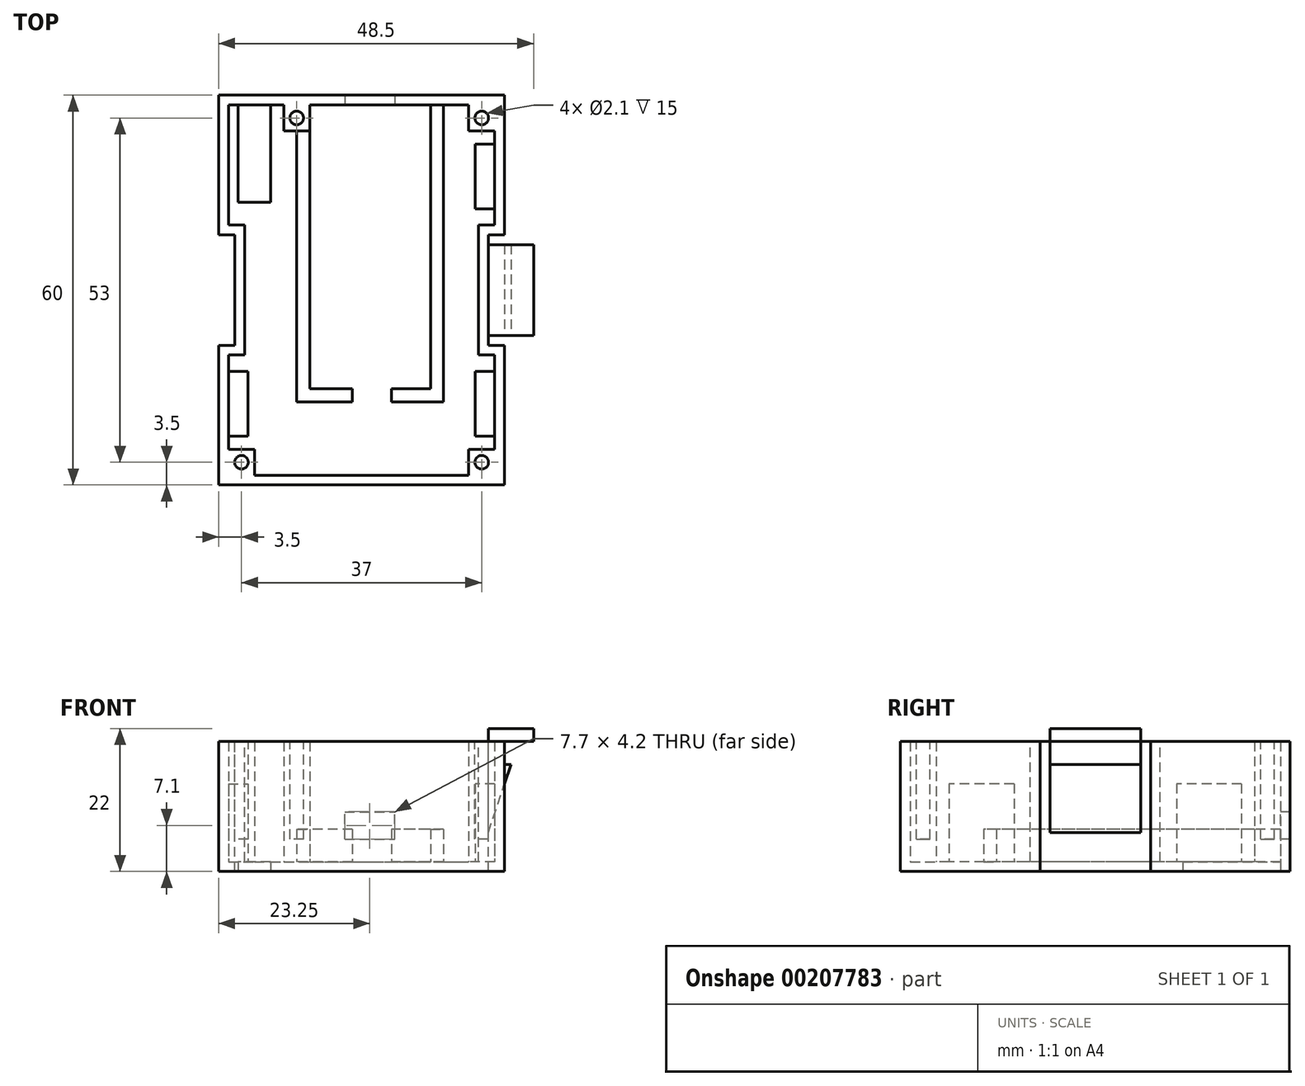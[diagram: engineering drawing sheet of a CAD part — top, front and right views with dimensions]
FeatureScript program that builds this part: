
annotation { "Feature Type Name" : "Feature", "Feature Type Description" : "" }
export const myFeature = defineFeature(function(context is Context, id is Id, definition is map)
    precondition{}
    {
        {
            var Q0;
            Q0=qCreatedBy(makeId("Top.planeOp"),FACE);
            var sketch = newSketch(context, id + "F0", { "sketchPlane" : qUnion([Q0])});
            skLineSegment(sketch, "E0.bottom", {"start": v(-22, 30) * mm, "end": v(22, 30) * mm});
            skLineSegment(sketch, "E0.top", {"start": v(-22, -30) * mm, "end": v(22, -30) * mm});
            skLineSegment(sketch, "E0.left", {"start": v(-22, 30) * mm, "end": v(-22, -30) * mm});
            skLineSegment(sketch, "E0.right", {"start": v(22, 30) * mm, "end": v(22, -30) * mm});
            skSolve(sketch);
        }
        {
            var Q0;
            Q0 = qSketchRegion(id + "F0", true);
            extrude(context, id + "F1", {"entities" : qUnion([Q0]), "depth" : 20 * mm});
        }
        {
            var Q0;
            Q0=makeQuery(id+"F1.opExtrude","CAP_FACE",FACE,{"disambiguationData":[OSD([sQuery(id+"F0.wireOp",EDGE,"E0.bottom"),sQuery(id+"F0.wireOp",EDGE,"E0.top"),sQuery(id+"F0.wireOp",EDGE,"E0.left"),sQuery(id+"F0.wireOp",EDGE,"E0.right")])],"isStart":false});
            var sketch = newSketch(context, id + "F2", { "sketchPlane" : qUnion([Q0])});
            skLineSegment(sketch, "E1.bottom", {"start": v(22, 8.5) * mm, "end": v(19.5, 8.5) * mm});
            skLineSegment(sketch, "E1.top", {"start": v(22, -8.5) * mm, "end": v(19.5, -8.5) * mm});
            skLineSegment(sketch, "E1.left", {"start": v(22, 8.5) * mm, "end": v(22, -8.5) * mm});
            skLineSegment(sketch, "E1.right", {"start": v(19.5, 8.5) * mm, "end": v(19.5, -8.5) * mm});
            skLineSegment(sketch, "E2.bottom", {"start": v(-22, 8.5) * mm, "end": v(-19.5, 8.5) * mm});
            skLineSegment(sketch, "E2.top", {"start": v(-22, -8.5) * mm, "end": v(-19.5, -8.5) * mm});
            skLineSegment(sketch, "E2.left", {"start": v(-22, 8.5) * mm, "end": v(-22, -8.5) * mm});
            skLineSegment(sketch, "E2.right", {"start": v(-19.5, 8.5) * mm, "end": v(-19.5, -8.5) * mm});
            skSolve(sketch);
        }
        {
            var Q0;
            Q0 = qSketchRegion(id + "F2", true);
            extrude(context, id + "F3", {"entities" : qUnion([Q0]), "operationType" : NewBodyOperationType.REMOVE, "oppositeDirection" : true, "depth" : 20 * mm});
        }
        {
            var Q0;
            Q0=makeQuery(id+"F1.opExtrude","CAP_FACE",FACE,{"disambiguationData":[OSD([sQuery(id+"F0.wireOp",EDGE,"E0.bottom"),sQuery(id+"F0.wireOp",EDGE,"E0.top"),sQuery(id+"F0.wireOp",EDGE,"E0.left"),sQuery(id+"F0.wireOp",EDGE,"E0.right")])],"isStart":false});
            shell(context, id + "F4", {"entities" : qUnion([Q0]), "thickness" : 1.5 * mm});
        }
        {
            var Q0;
            Q0=makeQuery(id+"F1.opExtrude","CAP_FACE",FACE,{"disambiguationData":[OSD([sQuery(id+"F0.wireOp",EDGE,"E0.bottom"),sQuery(id+"F0.wireOp",EDGE,"E0.top"),sQuery(id+"F0.wireOp",EDGE,"E0.left"),sQuery(id+"F0.wireOp",EDGE,"E0.right")])],"isStart":true});
            var sketch = newSketch(context, id + "F5", { "sketchPlane" : qUnion([Q0])});
            skLineSegment(sketch, "E3.bottom", {"start": v(-19, -28.5) * mm, "end": v(-14, -28.5) * mm});
            skLineSegment(sketch, "E3.top", {"start": v(-19, -13.5) * mm, "end": v(-14, -13.5) * mm});
            skLineSegment(sketch, "E3.left", {"start": v(-19, -28.5) * mm, "end": v(-19, -13.5) * mm});
            skLineSegment(sketch, "E3.right", {"start": v(-14, -28.5) * mm, "end": v(-14, -13.5) * mm});
            skSolve(sketch);
        }
        {
            var Q0;
            Q0 = qSketchRegion(id + "F5", true);
            extrude(context, id + "F6", {"entities" : qUnion([Q0]), "operationType" : NewBodyOperationType.REMOVE, "oppositeDirection" : true, "depth" : 2 * mm});
        }
        {
            var Q0;
            Q0=makeQuery(id+"F3.boolean.opBoolean","COPY",FACE,{"derivedFrom":makeQuery(id+"F3.opExtrude","SWEPT_FACE",FACE,{"disambiguationData":[OSD([sQuery(id+"F2.wireOp",EDGE,"E1.right")])]})});
            var sketch = newSketch(context, id + "F7", { "sketchPlane" : qUnion([Q0])});
            skLineSegment(sketch, "E4.bottom", {"start": v(-7, 20) * mm, "end": v(7, 20) * mm});
            skLineSegment(sketch, "E4.top", {"start": v(-7, 6) * mm, "end": v(7, 6) * mm});
            skLineSegment(sketch, "E4.left", {"start": v(-7, 20) * mm, "end": v(-7, 6) * mm});
            skLineSegment(sketch, "E4.right", {"start": v(7, 20) * mm, "end": v(7, 6) * mm});
            skLineSegment(sketch, "E5.top", {"start": v(-7, 22) * mm, "end": v(7, 22) * mm});
            skLineSegment(sketch, "E5.left", {"start": v(-7, 20) * mm, "end": v(-7, 22) * mm});
            skLineSegment(sketch, "E5.right", {"start": v(7, 20) * mm, "end": v(7, 22) * mm});
            skSolve(sketch);
        }
        {
            var Q0;
            Q0 = qSketchRegion(id + "F7", true);
            extrude(context, id + "F8", {"entities" : qUnion([Q0]), "operationType" : NewBodyOperationType.ADD, "depth" : 7 * mm});
        }
        {
            var Q0;
            Q0=makeQuery(id+"F8.opExtrude","SWEPT_FACE",FACE,{"disambiguationData":[OSD([sQuery(id+"F7.wireOp",EDGE,"E4.left"),sQuery(id+"F7.wireOp",EDGE,"E5.left")])]});
            var sketch = newSketch(context, id + "F9", { "sketchPlane" : qUnion([Q0])});
            skLineSegment(sketch, "E6", {"start": v(19.5, 6) * mm, "end": v(23, 16.5) * mm});
            skLineSegment(sketch, "E7", {"start": v(23, 16.5) * mm, "end": v(22, 16.5) * mm});
            skLineSegment(sketch, "E8", {"start": v(22, 16.5) * mm, "end": v(22, 20) * mm});
            skLineSegment(sketch, "E9", {"start": v(22, 20) * mm, "end": v(26.5, 20) * mm});
            skLineSegment(sketch, "E10", {"start": v(26.5, 20) * mm, "end": v(26.5, 6) * mm});
            skLineSegment(sketch, "E11", {"start": v(26.5, 6) * mm, "end": v(19.5, 6) * mm});
            skSolve(sketch);
        }
        {
            var Q0;
            Q0 = qSketchRegion(id + "F9", true);
            extrude(context, id + "F10", {"entities" : qUnion([Q0]), "operationType" : NewBodyOperationType.REMOVE, "oppositeDirection" : true, "depth" : 14 * mm});
        }
        {
            var Q0;
            Q0=makeQuery(id+"F4.opShell","OFFSET_FACE",FACE,{"disambiguationData":[OSD([sQuery(id+"F0.wireOp",EDGE,"E0.bottom"),sQuery(id+"F0.wireOp",EDGE,"E0.top"),sQuery(id+"F0.wireOp",EDGE,"E0.left"),sQuery(id+"F0.wireOp",EDGE,"E0.right")])]});
            var sketch = newSketch(context, id + "F11", { "sketchPlane" : qUnion([Q0])});
            skLineSegment(sketch, "E12.bottom", {"start": v(20.5, 28.5) * mm, "end": v(16.5, 28.5) * mm});
            skLineSegment(sketch, "E12.top", {"start": v(20.5, 24.5) * mm, "end": v(16.5, 24.5) * mm});
            skLineSegment(sketch, "E12.left", {"start": v(20.5, 28.5) * mm, "end": v(20.5, 24.5) * mm});
            skLineSegment(sketch, "E12.right", {"start": v(16.5, 28.5) * mm, "end": v(16.5, 24.5) * mm});
            skLineSegment(sketch, "E13.bottom", {"start": v(20.5, -28.5) * mm, "end": v(16.5, -28.5) * mm});
            skLineSegment(sketch, "E13.top", {"start": v(20.5, -24.5) * mm, "end": v(16.5, -24.5) * mm});
            skLineSegment(sketch, "E13.left", {"start": v(20.5, -28.5) * mm, "end": v(20.5, -24.5) * mm});
            skLineSegment(sketch, "E13.right", {"start": v(16.5, -28.5) * mm, "end": v(16.5, -24.5) * mm});
            skLineSegment(sketch, "E14.bottom", {"start": v(-20.5, -28.5) * mm, "end": v(-16.5, -28.5) * mm});
            skLineSegment(sketch, "E14.top", {"start": v(-20.5, -24.5) * mm, "end": v(-16.5, -24.5) * mm});
            skLineSegment(sketch, "E14.left", {"start": v(-20.5, -28.5) * mm, "end": v(-20.5, -24.5) * mm});
            skLineSegment(sketch, "E14.right", {"start": v(-16.5, -28.5) * mm, "end": v(-16.5, -24.5) * mm});
            skLineSegment(sketch, "E15.bottom", {"start": v(-12, 28.5) * mm, "end": v(-8, 28.5) * mm});
            skLineSegment(sketch, "E15.top", {"start": v(-12, 24.5) * mm, "end": v(-8, 24.5) * mm});
            skLineSegment(sketch, "E15.left", {"start": v(-12, 28.5) * mm, "end": v(-12, 24.5) * mm});
            skLineSegment(sketch, "E15.right", {"start": v(-8, 28.5) * mm, "end": v(-8, 24.5) * mm});
            skSolve(sketch);
        }
        {
            var Q0;
            Q0 = qSketchRegion(id + "F11", true);
            var Q1;
            Q1=makeQuery(id+"F1.opExtrude","CAP_FACE",FACE,{"disambiguationData":[OSD([sQuery(id+"F0.wireOp",EDGE,"E0.bottom"),sQuery(id+"F0.wireOp",EDGE,"E0.top"),sQuery(id+"F0.wireOp",EDGE,"E0.left"),sQuery(id+"F0.wireOp",EDGE,"E0.right")])],"isStart":false});
            extrude(context, id + "F12", {"entities" : qUnion([Q0]), "operationType" : NewBodyOperationType.ADD, "endBound" : BoundingType.UP_TO_SURFACE, "endBoundEntityFace" : qUnion([Q1]), "depth" : 18.5 * mm});
        }
        {
            var Q0;
            {var subQ0=sQuery(id+"F0.wireOp",EDGE,"E0.right");var subQ1=sQuery(id+"F0.wireOp",EDGE,"E0.left");var subQ2=sQuery(id+"F0.wireOp",EDGE,"E0.top");var subQ3=sQuery(id+"F0.wireOp",EDGE,"E0.bottom");Q0=makeQuery(id+"F12.boolean.opBoolean","MERGE",FACE,{"derivedFrom":[makeQuery(id+"F1.opExtrude","CAP_FACE",FACE,{"disambiguationData":[OSD([subQ3,subQ2,subQ1,subQ0])],"isStart":false}),makeQuery(id+"F12.opExtrude","CAP_FACE",FACE,{"disambiguationData":[OSD([subQ3,subQ2,subQ1,subQ0]),ownerDisambiguation([makeQuery(id+"F12.opExtrude","SWEPT_BODY",BODY,{"disambiguationData":[OSD([sQuery(id+"F11.wireOp",EDGE,"E12.bottom"),sQuery(id+"F11.wireOp",EDGE,"E12.top"),sQuery(id+"F11.wireOp",EDGE,"E12.left"),sQuery(id+"F11.wireOp",EDGE,"E12.right")])]})])],"isStart":false}),makeQuery(id+"F12.opExtrude","CAP_FACE",FACE,{"disambiguationData":[OSD([subQ3,subQ2,subQ1,subQ0]),ownerDisambiguation([makeQuery(id+"F12.opExtrude","SWEPT_BODY",BODY,{"disambiguationData":[OSD([sQuery(id+"F11.wireOp",EDGE,"E13.bottom"),sQuery(id+"F11.wireOp",EDGE,"E13.top"),sQuery(id+"F11.wireOp",EDGE,"E13.left"),sQuery(id+"F11.wireOp",EDGE,"E13.right")])]})])],"isStart":false}),makeQuery(id+"F12.opExtrude","CAP_FACE",FACE,{"disambiguationData":[OSD([subQ3,subQ2,subQ1,subQ0]),ownerDisambiguation([makeQuery(id+"F12.opExtrude","SWEPT_BODY",BODY,{"disambiguationData":[OSD([sQuery(id+"F11.wireOp",EDGE,"E14.bottom"),sQuery(id+"F11.wireOp",EDGE,"E14.top"),sQuery(id+"F11.wireOp",EDGE,"E14.left"),sQuery(id+"F11.wireOp",EDGE,"E14.right")])]})])],"isStart":false}),makeQuery(id+"F12.opExtrude","CAP_FACE",FACE,{"disambiguationData":[OSD([subQ3,subQ2,subQ1,subQ0]),ownerDisambiguation([makeQuery(id+"F12.opExtrude","SWEPT_BODY",BODY,{"disambiguationData":[OSD([sQuery(id+"F11.wireOp",EDGE,"E15.bottom"),sQuery(id+"F11.wireOp",EDGE,"E15.top"),sQuery(id+"F11.wireOp",EDGE,"E15.left"),sQuery(id+"F11.wireOp",EDGE,"E15.right")])]})])],"isStart":false})]});}
            var sketch = newSketch(context, id + "F13", { "sketchPlane" : qUnion([Q0])});
            skCircle(sketch, "E16", {"center": v(-10, 26.5) * mm, "radius": 1.05 * mm});
            skPoint(sketch, "E16.centerSnap0", {"position": v(-12, 26.5) * mm});
            skCircle(sketch, "E17", {"center": v(18.5, 26.5) * mm, "radius": 1.05 * mm});
            skPoint(sketch, "E17.centerSnap0", {"position": v(18.5, 24.5) * mm});
            skPoint(sketch, "E17.centerSnap1", {"position": v(16.5, 26.5) * mm});
            skCircle(sketch, "E18", {"center": v(18.5, -26.5) * mm, "radius": 1.05 * mm});
            skPoint(sketch, "E18.centerSnap0", {"position": v(16.5, -26.5) * mm});
            skPoint(sketch, "E18.centerSnap1", {"position": v(18.5, -24.5) * mm});
            skCircle(sketch, "E19", {"center": v(-18.5, -26.5) * mm, "radius": 1.05 * mm});
            skPoint(sketch, "E19.centerSnap0", {"position": v(-16.5, -26.5) * mm});
            skPoint(sketch, "E19.centerSnap1", {"position": v(-18.5, -24.5) * mm});
            skPoint(sketch, "E20", {"position": v(-10, 24.5) * mm});
            skSolve(sketch);
        }
        {
            var Q0;
            Q0 = qSketchRegion(id + "F13", true);
            extrude(context, id + "F14", {"entities" : qUnion([Q0]), "operationType" : NewBodyOperationType.REMOVE, "oppositeDirection" : true, "depth" : 15 * mm});
        }
        {
            var Q0;
            {var subQ4=sQuery(id+"F0.wireOp",EDGE,"E0.bottom");var subQ5=sQuery(id+"F11.wireOp",EDGE,"E12.right");Q0=makeQuery(id+"F12.boolean.opBoolean","SPLIT",FACE,{"disambiguationData":[TD([makeQuery(id+"F12.opExtrude","SWEPT_FACE",FACE,{"disambiguationData":[OSD([subQ5])]})])],"derivedFrom":makeQuery(id+"F6.boolean.opBoolean","MERGE",FACE,{"derivedFrom":[makeQuery(id+"F4.opShell","OFFSET_FACE",FACE,{"disambiguationData":[OSD([subQ4])]}),makeQuery(id+"F6.opExtrude","SWEPT_FACE",FACE,{"disambiguationData":[OSD([sQuery(id+"F5.wireOp",EDGE,"E3.bottom")])]})]})});}
            var sketch = newSketch(context, id + "F15", { "sketchPlane" : qUnion([Q0])});
            skLineSegment(sketch, "E21.bottom", {"start": v(-2.6, 5) * mm, "end": v(5.1, 5) * mm});
            skLineSegment(sketch, "E21.top", {"start": v(-2.6, 9.2) * mm, "end": v(5.1, 9.2) * mm});
            skLineSegment(sketch, "E21.left", {"start": v(-2.6, 5) * mm, "end": v(-2.6, 9.2) * mm});
            skLineSegment(sketch, "E21.right", {"start": v(5.1, 5) * mm, "end": v(5.1, 9.2) * mm});
            skSolve(sketch);
        }
        {
            var Q0;
            Q0 = qSketchRegion(id + "F15", true);
            extrude(context, id + "F16", {"entities" : qUnion([Q0]), "operationType" : NewBodyOperationType.REMOVE, "endBound" : BoundingType.UP_TO_NEXT, "oppositeDirection" : true, "depth" : 25 * mm});
        }
        {
            var Q0;
            Q0=makeQuery(id+"F4.opShell","OFFSET_FACE",FACE,{"disambiguationData":[OSD([sQuery(id+"F0.wireOp",EDGE,"E0.bottom"),sQuery(id+"F0.wireOp",EDGE,"E0.top"),sQuery(id+"F0.wireOp",EDGE,"E0.left"),sQuery(id+"F0.wireOp",EDGE,"E0.right")])]});
            var sketch = newSketch(context, id + "F17", { "sketchPlane" : qUnion([Q0])});
            skLineSegment(sketch, "E22.bottom", {"start": v(10.6, 28.5) * mm, "end": v(12.6, 28.5) * mm});
            skLineSegment(sketch, "E22.top", {"start": v(10.6, -15.2) * mm, "end": v(12.6, -15.2) * mm});
            skLineSegment(sketch, "E22.left", {"start": v(10.6, 28.5) * mm, "end": v(10.6, -15.2) * mm});
            skLineSegment(sketch, "E22.right", {"start": v(12.6, 28.5) * mm, "end": v(12.6, -15.2) * mm});
            skLineSegment(sketch, "E23.bottom", {"start": v(-8, 24.5) * mm, "end": v(-10, 24.5) * mm});
            skLineSegment(sketch, "E23.top", {"start": v(-8, -15.2) * mm, "end": v(-10, -15.2) * mm});
            skLineSegment(sketch, "E23.left", {"start": v(-8, 24.5) * mm, "end": v(-8, -15.2) * mm});
            skLineSegment(sketch, "E23.right", {"start": v(-10, 24.5) * mm, "end": v(-10, -15.2) * mm});
            skLineSegment(sketch, "E24.bottom", {"start": v(12.6, -15.2) * mm, "end": v(-10, -15.2) * mm});
            skLineSegment(sketch, "E24.top", {"start": v(12.6, -17.2) * mm, "end": v(-10, -17.2) * mm});
            skLineSegment(sketch, "E24.left", {"start": v(12.6, -15.2) * mm, "end": v(12.6, -17.2) * mm});
            skLineSegment(sketch, "E24.right", {"start": v(-10, -15.2) * mm, "end": v(-10, -17.2) * mm});
            skSolve(sketch);
        }
        {
            var Q0;
            Q0 = qSketchRegion(id + "F17", true);
            extrude(context, id + "F18", {"entities" : qUnion([Q0]), "operationType" : NewBodyOperationType.ADD, "depth" : 5 * mm});
        }
        {
            var Q0;
            {var subQ2=sQuery(id+"F0.wireOp",EDGE,"E0.right");var subQ3=sQuery(id+"F0.wireOp",EDGE,"E0.left");var subQ4=sQuery(id+"F0.wireOp",EDGE,"E0.top");var subQ5=sQuery(id+"F0.wireOp",EDGE,"E0.bottom");Q0=makeQuery(id+"F18.boolean.opBoolean","SPLIT",FACE,{"disambiguationData":[TD([makeQuery(id+"F4.opShell","OFFSET_FACE",FACE,{"disambiguationData":[OSD([subQ4])]})])],"derivedFrom":makeQuery(id+"F4.opShell","OFFSET_FACE",FACE,{"disambiguationData":[OSD([subQ5,subQ4,subQ3,subQ2])]})});}
            var sketch = newSketch(context, id + "F19", { "sketchPlane" : qUnion([Q0])});
            skLineSegment(sketch, "E25.bottom", {"start": v(20.5, 22.5) * mm, "end": v(17.5, 22.5) * mm});
            skLineSegment(sketch, "E25.top", {"start": v(20.5, 12.5) * mm, "end": v(17.5, 12.5) * mm});
            skLineSegment(sketch, "E25.left", {"start": v(20.5, 22.5) * mm, "end": v(20.5, 12.5) * mm});
            skLineSegment(sketch, "E25.right", {"start": v(17.5, 22.5) * mm, "end": v(17.5, 12.5) * mm});
            skLineSegment(sketch, "E26.bottom", {"start": v(20.5, -12.5) * mm, "end": v(17.5, -12.5) * mm});
            skLineSegment(sketch, "E26.top", {"start": v(20.5, -22.5) * mm, "end": v(17.5, -22.5) * mm});
            skLineSegment(sketch, "E26.left", {"start": v(20.5, -12.5) * mm, "end": v(20.5, -22.5) * mm});
            skLineSegment(sketch, "E26.right", {"start": v(17.5, -12.5) * mm, "end": v(17.5, -22.5) * mm});
            skLineSegment(sketch, "E27.bottom", {"start": v(-20.5, -12.5) * mm, "end": v(-17.5, -12.5) * mm});
            skLineSegment(sketch, "E27.top", {"start": v(-20.5, -22.5) * mm, "end": v(-17.5, -22.5) * mm});
            skLineSegment(sketch, "E27.left", {"start": v(-20.5, -12.5) * mm, "end": v(-20.5, -22.5) * mm});
            skLineSegment(sketch, "E27.right", {"start": v(-17.5, -12.5) * mm, "end": v(-17.5, -22.5) * mm});
            skSolve(sketch);
        }
        {
            var Q0;
            Q0 = qSketchRegion(id + "F19", true);
            extrude(context, id + "F20", {"entities" : qUnion([Q0]), "operationType" : NewBodyOperationType.ADD, "depth" : 12 * mm});
        }
        {
            var Q0;
            {var subQ2=sQuery(id+"F0.wireOp",EDGE,"E0.right");var subQ3=sQuery(id+"F0.wireOp",EDGE,"E0.left");var subQ4=sQuery(id+"F0.wireOp",EDGE,"E0.top");var subQ5=sQuery(id+"F0.wireOp",EDGE,"E0.bottom");Q0=makeQuery(id+"F18.boolean.opBoolean","SPLIT",FACE,{"disambiguationData":[TD([makeQuery(id+"F4.opShell","OFFSET_FACE",FACE,{"disambiguationData":[OSD([subQ4])]})])],"derivedFrom":makeQuery(id+"F4.opShell","OFFSET_FACE",FACE,{"disambiguationData":[OSD([subQ5,subQ4,subQ3,subQ2])]})});}
            var sketch = newSketch(context, id + "F21", { "sketchPlane" : qUnion([Q0])});
            skLineSegment(sketch, "E28.bottom", {"start": v(-1.4, -17.2) * mm, "end": v(4.6, -17.2) * mm});
            skLineSegment(sketch, "E28.top", {"start": v(-1.4, -15.2) * mm, "end": v(4.6, -15.2) * mm});
            skLineSegment(sketch, "E28.left", {"start": v(-1.4, -17.2) * mm, "end": v(-1.4, -15.2) * mm});
            skLineSegment(sketch, "E28.right", {"start": v(4.6, -17.2) * mm, "end": v(4.6, -15.2) * mm});
            skSolve(sketch);
        }
        {
            var Q0;
            Q0 = qSketchRegion(id + "F21", true);
            extrude(context, id + "F22", {"entities" : qUnion([Q0]), "operationType" : NewBodyOperationType.REMOVE, "depth" : 10 * mm});
        }
    });
